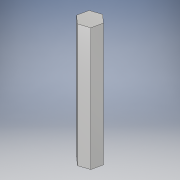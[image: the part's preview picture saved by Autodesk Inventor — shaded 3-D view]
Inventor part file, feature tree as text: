
AUTODESK INVENTOR PART (.ipt)
format: ipt  version: 2018 (Build 220112000, 112)  size: 101,376 bytes
history: native  units: in
note: dims shown in document units (in); Inventor stores cm internally (conversion verified against a paired STEP export)
features: extrude x1, sketch x1
ambient origin geometry x8: Origin, YZ Plane, XZ Plane, XY Plane, X Axis, Y Axis, Z Axis, Center Point
bodies: Solid1 (feature_tree)
feature tree (2):
  extrude  "Extrusion1"  Depth=2.5in TaperAngle=0.0deg
  sketch  "Sketch1"  dims[d0=0.375in d1=2.5in d2=0.0in]
